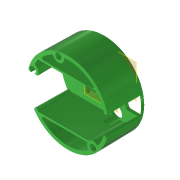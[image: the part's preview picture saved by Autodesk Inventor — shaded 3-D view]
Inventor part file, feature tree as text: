
AUTODESK INVENTOR PART (.ipt)
format: ipt  version: 2022 (Build 260153000, 153)  size: 642,560 bytes
history: native  units: in
note: dims shown in document units (in); Inventor stores cm internally (conversion verified against a paired STEP export)
features: extrude x14, sketch x14, other x9, reference x7, plane x5, projected_geometry x2, fillet x1
ambient origin geometry x8: Origin, YZ Plane, XZ Plane, XY Plane, X Axis, Y Axis, Z Axis, Center Point
bodies: Solid1 (feature_tree)
feature tree (52):
  plane  "Arbeitsebene6"
  extrude  "Extrusion1"  Depth=0.315in
  extrude  "Extrusion2"  Depth=1.0in
  plane  "Arbeitsebene3"
  extrude  "Extrusion6"  Depth=0.1102in
  plane  "Arbeitsebene2"
  extrude  "Extrusion7"  Depth=0.0787in
  extrude  "Extrusion10"  Depth=0.0394in TaperAngle=0.0deg
  plane  "Arbeitsebene7"
  sketch  "Skizze16"  dims[d81=0.0591in d82=0.3937in d83=0.0069in]
  plane  "Arbeitsebene5"
  extrude  "Extrusion14"  Depth=0.3937in
  extrude  "Extrusion15"  Depth=0.3937in
  extrude  "Extrusion17"  TaperAngle=0.0deg  [1 undecoded]
  extrude  "Extrusion18"  Depth=0.1575in
  extrude  "Extrusion19"  Depth=0.1575in
  extrude  "Extrusion20"  Depth=0.8465in TaperAngle=0.0deg
  fillet  "Rundung2"  Radius=0.1614in
  extrude  "Extrusion21"  Depth=0.1614in
  extrude  "Extrusion22"  Depth=0.315in
  extrude  "Extrusion23"  Depth=0.0591in
  sketch  "Sketch1"  dims[d0=0.0787in d1=-0.0069in d2=0.315in]
  sketch  "Sketch2"  dims[d3=0.3189in d4=1.0in d5=-0.0137in]
  sketch  "Sketch8"  dims[d33=0.1102in d34=0.1102in]
  sketch  "Sketch9"  dims[d35=0.0in d36=0.0in d37=0.0787in]
  sketch  "Skizze12"  dims[d38=0.0004in d39=-0.0069in d51=0.0394in d52=0.0in]
  sketch  "Skizze17"  dims[d89=0.3937in d90=-0.0069in d91=0.0787in]
  reference  "Referenz44"
  reference  "Referenz45"
  projected_geometry  "Projizierte Kontur4"
  sketch  "Skizze19"  dims[d92=0.0787in d93=0.0in]
  sketch  "Skizze20"  dims[d94=0.0in d104=0.1575in]
  sketch  "Skizze21"  dims[d105=0.1575in d106=0.1575in]
  sketch  "Skizze22"  dims[d107=0.0001in d108=-0.0069in d109=0.8465in d110=0.0in d111=0.1614in]
  reference  "Referenz46"
  sketch  "Skizze23"  dims[d112=0.1614in d113=0.1614in]
  sketch  "Skizze24"  dims[d114=0.1969in d115=-0.0069in d116=0.315in]
  projected_geometry  "Projizierte Kontur5"
  reference  "Referenz47"
  sketch  "Skizze25"  dims[d117=0.315in d118=0.0069in d119=0.0394in d120=0.0394in d122=0.9055in d123=0.4528in d124=1.8701in d125=0.2756in d126=0.4724in d127=0.5906in d128=0.0394in d129=0.0in d130=0.315in d131=0.315in d132=0.1102in d133=0.1102in d134=0.0in d135=0.0in d136=1.4961in d137=0.315in d138=0.315in d139=0.0591in d140=0.0in d78=0.0197in d79=0.0344in d80=0.0197in d95=0.0197in d96=0.0344in d97=0.0197in d98=0.0344in]
  reference  "Referenz48"
  reference  "Referenz49"
  reference  "Referenz50"
  other  "Matchboxscope_VCM_v1.iam"
  other  "Matchboxscope_bottom_v0:2"
  other  "Matchboxscope_middle2_m12VCMLens_v2:2"
  other  "Spectroscope_v0.iam"
  other  "IM_Matchboxscope_plate:1"
  other  "Assembly_Matchboxscope_injectionmolded_ESPectrometer.iam"
  other  "IM_Matchboxscope_plate:2"
  other  "IM_Lensholder:1"
  other  "DIN 912 - ersetzt durch DIN EN ISO 4762 M3 x 10:3"
note: 1 required parameter value undecoded (feature->parameter linkage not recoverable at this tier; creation-order binding heuristic only, values carry confidence <= 0.55)
